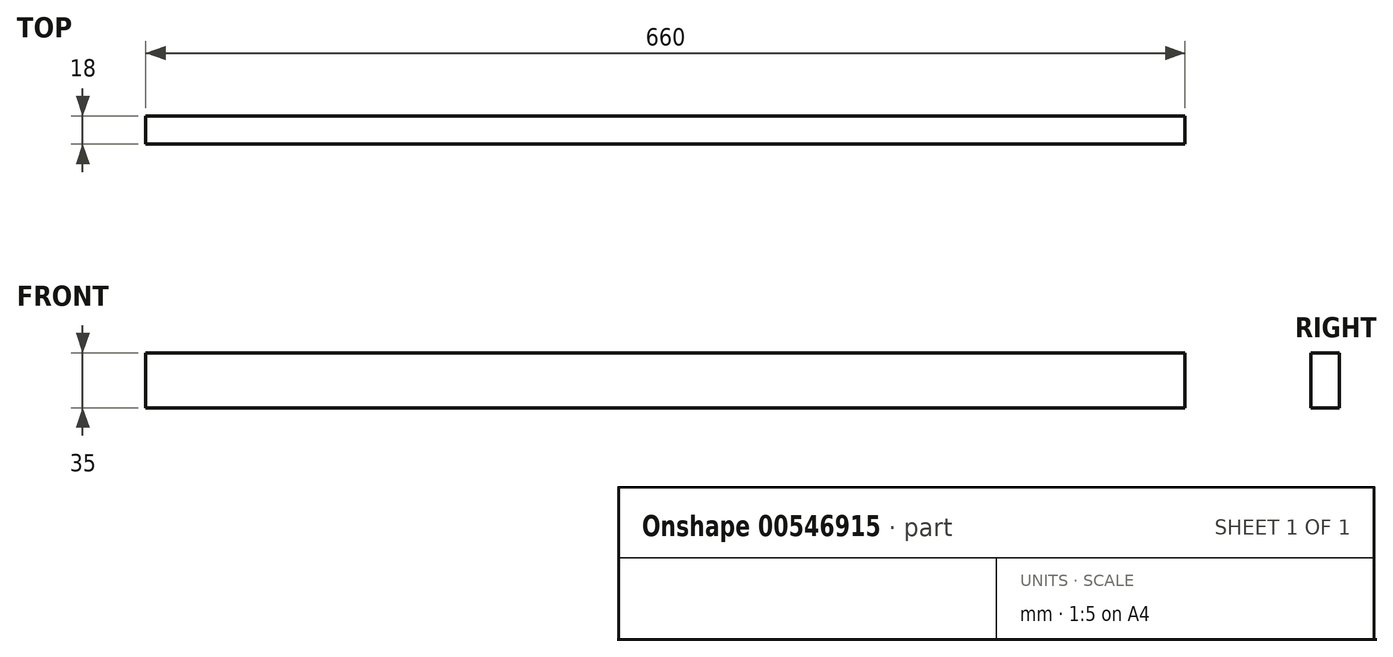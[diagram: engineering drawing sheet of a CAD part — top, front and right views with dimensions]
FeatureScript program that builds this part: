
annotation { "Feature Type Name" : "Feature", "Feature Type Description" : "" }
export const myFeature = defineFeature(function(context is Context, id is Id, definition is map)
    precondition{}
    {
        {
            var Q0;
            Q0=qCreatedBy(makeId("Front.planeOp"),FACE);
            var sketch = newSketch(context, id + "F0", { "sketchPlane" : qUnion([Q0])});
            skLineSegment(sketch, "E0.bottom", {"start": v(-297.53, -156.09) * mm, "end": v(362.47, -156.09) * mm});
            skLineSegment(sketch, "E0.top", {"start": v(-297.53, -121.09) * mm, "end": v(362.47, -121.09) * mm});
            skLineSegment(sketch, "E0.left", {"start": v(-297.53, -156.09) * mm, "end": v(-297.53, -121.09) * mm});
            skLineSegment(sketch, "E0.right", {"start": v(362.47, -156.09) * mm, "end": v(362.47, -121.09) * mm});
            skSolve(sketch);
        }
        {
            var Q0;
            Q0=makeQuery(id+"F0.imprint","IMPRINT",FACE,{"disambiguationData":[TD([[makeQuery(id+"F0.imprint","IMPRINT",EDGE,{"derivedFrom":sQuery(id+"F0.wireOp",EDGE,"E0.bottom")}),1.0]])]});
            extrude(context, id + "F1", {"entities" : qUnion([Q0]), "depth" : 18 * mm, "offsetDistance" : 25 * mm});
        }
    });
